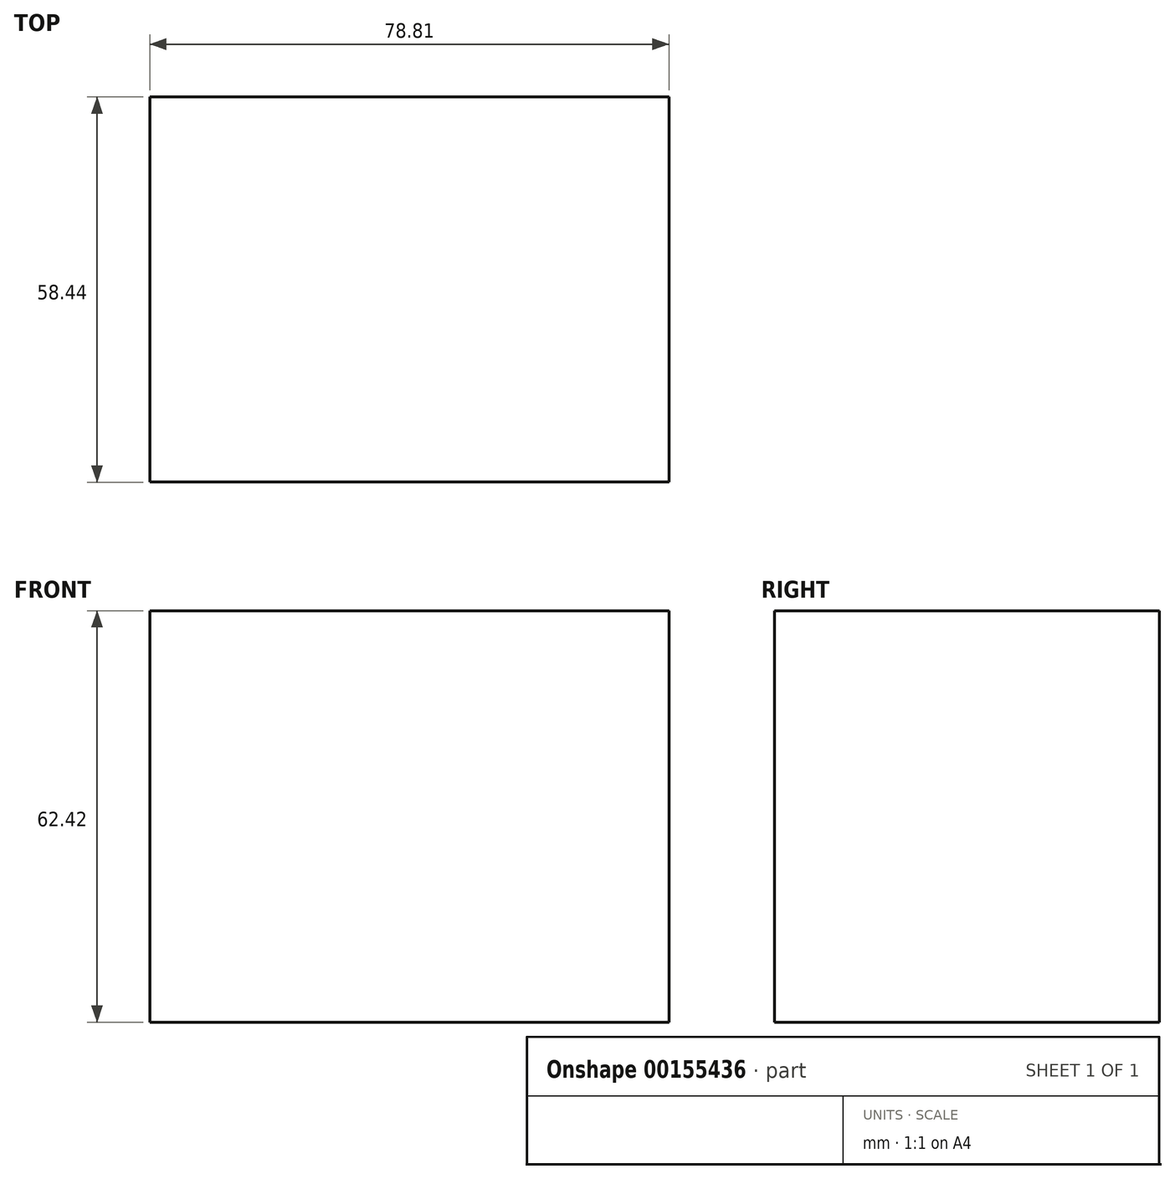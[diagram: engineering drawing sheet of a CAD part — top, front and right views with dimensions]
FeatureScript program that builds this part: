
annotation { "Feature Type Name" : "Feature", "Feature Type Description" : "" }
export const myFeature = defineFeature(function(context is Context, id is Id, definition is map)
    precondition{}
    {
        {
            var Q0;
            Q0=qCreatedBy(makeId("Front.planeOp"),FACE);
            var sketch = newSketch(context, id + "F1", { "sketchPlane" : qUnion([Q0])});
            skLineSegment(sketch, "E0.bottom", {"start": v(-30.96, -17.85) * mm, "end": v(47.85, -17.85) * mm});
            skLineSegment(sketch, "E0.top", {"start": v(-30.96, 44.57) * mm, "end": v(47.85, 44.57) * mm});
            skLineSegment(sketch, "E0.left", {"start": v(-30.96, -17.85) * mm, "end": v(-30.96, 44.57) * mm});
            skLineSegment(sketch, "E0.right", {"start": v(47.85, -17.85) * mm, "end": v(47.85, 44.57) * mm});
            skSolve(sketch);
        }
        {
            var Q0;
            Q0=makeQuery(id+"F1.imprint","IMPRINT",FACE,{"disambiguationData":[TD([[makeQuery(id+"F1.imprint","IMPRINT",EDGE,{"derivedFrom":sQuery(id+"F1.wireOp",EDGE,"E0.bottom")}),1.0]])]});
            extrude(context, id + "F0", {"entities" : qUnion([Q0]), "depth" : 58.44 * mm});
        }
    });
